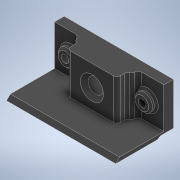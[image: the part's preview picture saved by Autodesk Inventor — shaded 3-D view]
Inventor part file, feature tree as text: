
AUTODESK INVENTOR PART (.ipt)
format: ipt  version: 2022 (Build 260153000, 153)  size: 585,216 bytes
history: native  units: mm
features: extrude x6, sketch x3, chamfer x3, fillet x3, projected_geometry x2, other x1
ambient origin geometry x8: Origin, YZ Plane, XZ Plane, XY Plane, X Axis, Y Axis, Z Axis, Center Point
bodies: Body1 (feature_tree)
feature tree (18):
  other  "Твердое тело1"
  sketch  "Эскиз1"
  extrude  "Выдавливание1"  Depth=2.0mm
  extrude  "Выдавливание2"  Depth=2.0mm
  extrude  "Выдавливание3"  Depth=20.0mm
  chamfer  "Фаска1"  Distance=5.5mm
  extrude  "Выдавливание4"  Depth=5.5mm
  fillet  "Сопряжение1"  Radius=14.2mm
  extrude  "Выдавливание5"  Depth=7.0mm
  chamfer  "Фаска2"  Distance=7.0mm
  extrude  "Выдавливание6"  Depth=7.0mm TaperAngle=0.0deg
  chamfer  "Фаска3"  Distance=1.0mm
  fillet  "Сопряжение2"  Radius=4.3mm
  fillet  "Сопряжение3"  Radius=1.0mm
  sketch  "Эскиз2"
  sketch  "Эскиз3"
  projected_geometry  "Спроецированная петля1"
  projected_geometry  "Спроецированная петля2"
